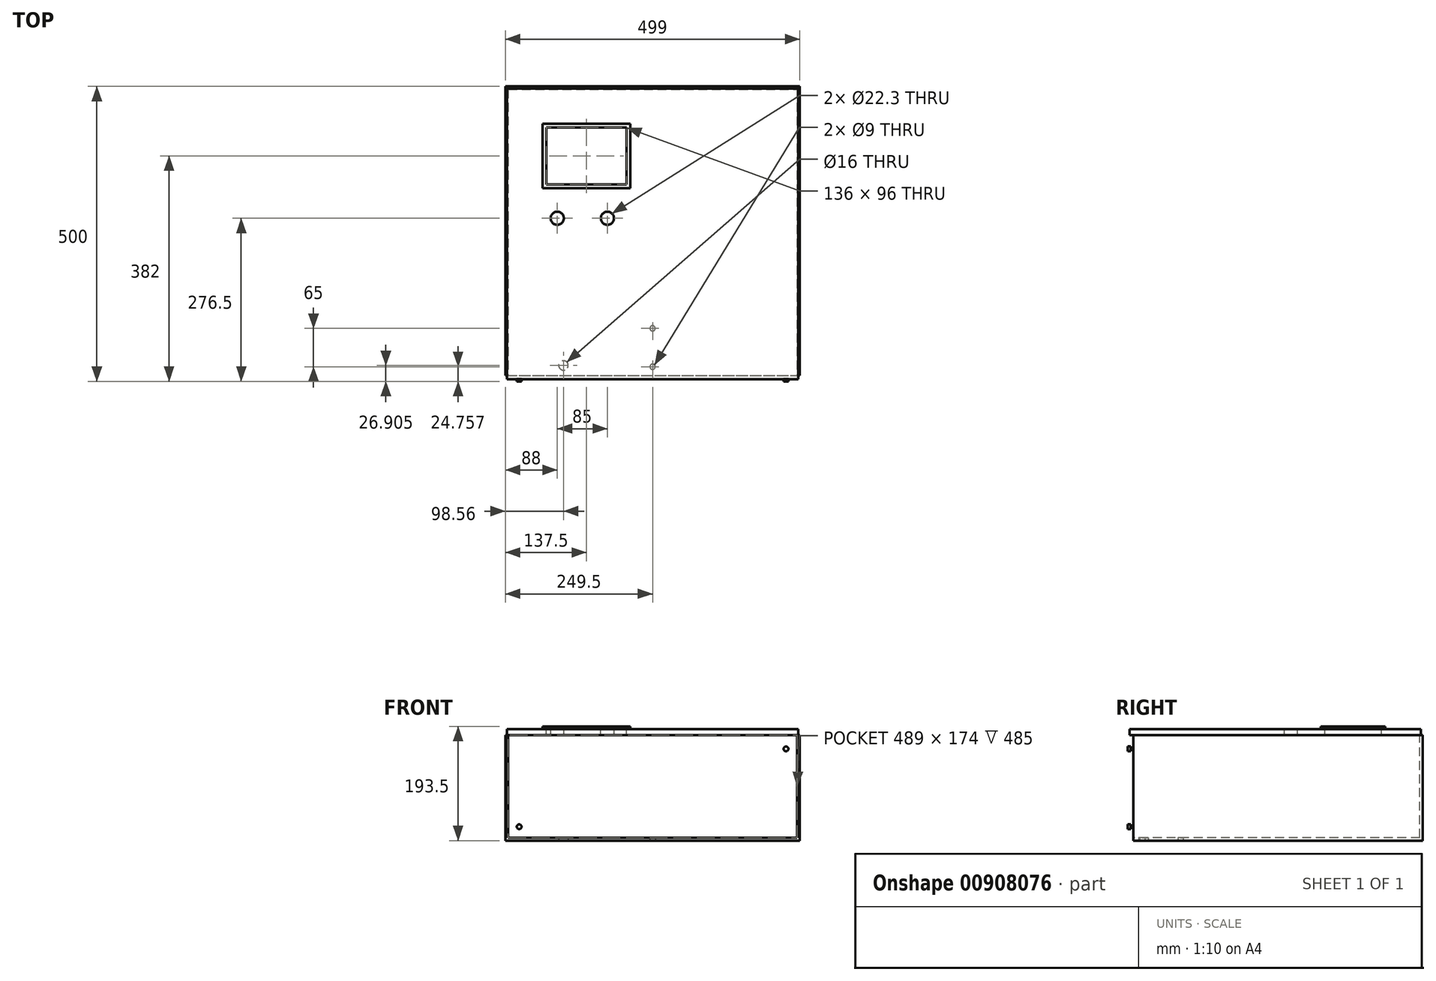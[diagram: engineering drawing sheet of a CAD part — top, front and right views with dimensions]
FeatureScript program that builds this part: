
annotation { "Feature Type Name" : "Feature", "Feature Type Description" : "" }
export const myFeature = defineFeature(function(context is Context, id is Id, definition is map)
    precondition{}
    {
        {
            var Q0;
            Q0=qCreatedBy(makeId("Top.planeOp"),FACE);
            var sketch = newSketch(context, id + "F0", { "sketchPlane" : qUnion([Q0])});
            skLineSegment(sketch, "E0.bottom", {"start": v(-249.5, 250) * mm, "end": v(249.5, 250) * mm});
            skLineSegment(sketch, "E0.top", {"start": v(-249.5, -250) * mm, "end": v(249.5, -250) * mm});
            skLineSegment(sketch, "E0.left", {"start": v(-249.5, 250) * mm, "end": v(-249.5, -250) * mm});
            skLineSegment(sketch, "E0.right", {"start": v(249.5, 250) * mm, "end": v(249.5, -250) * mm});
            skPoint(sketch, "E0.middle", {"position": v(0, 0) * mm});
            skSolve(sketch);
        }
        {
            var Q0;
            Q0=makeQuery(id+"F0.imprint","IMPRINT",FACE,{"disambiguationData":[TD([[makeQuery(id+"F0.imprint","IMPRINT",EDGE,{"derivedFrom":sQuery(id+"F0.wireOp",EDGE,"E0.bottom")}),-1.0]])]});
            extrude(context, id + "F1", {"entities" : qUnion([Q0]), "oppositeDirection" : true, "depth" : 179 * mm, "offsetDistance" : 25 * mm});
        }
        {
            var Q0;
            Q0=makeQuery(id+"F1.opExtrude","CAP_FACE",FACE,{"disambiguationData":[OSD([sQuery(id+"F0.wireOp",EDGE,"E0.bottom"),sQuery(id+"F0.wireOp",EDGE,"E0.top"),sQuery(id+"F0.wireOp",EDGE,"E0.left"),sQuery(id+"F0.wireOp",EDGE,"E0.right")])],"isStart":true});
            shell(context, id + "F2", {"entities" : qUnion([Q0]), "thickness" : 5 * mm});
        }
        {
            var Q0;
            Q0=qCreatedBy(makeId("Top.planeOp"),FACE);
            var sketch = newSketch(context, id + "F3", { "sketchPlane" : qUnion([Q0])});
            skLineSegment(sketch, "E1.bottom", {"start": v(-246.5, 246.5) * mm, "end": v(246.5, 246.5) * mm});
            skLineSegment(sketch, "E1.top", {"start": v(-246.5, -246.5) * mm, "end": v(246.5, -246.5) * mm});
            skLineSegment(sketch, "E1.left", {"start": v(-246.5, 246.5) * mm, "end": v(-246.5, -246.5) * mm});
            skLineSegment(sketch, "E1.right", {"start": v(246.5, 246.5) * mm, "end": v(246.5, -246.5) * mm});
            skSolve(sketch);
        }
        {
            var Q0;
            Q0=makeQuery(id+"F3.imprint","IMPRINT",FACE,{"disambiguationData":[TD([[makeQuery(id+"F3.imprint","IMPRINT",EDGE,{"derivedFrom":sQuery(id+"F3.wireOp",EDGE,"E1.bottom")}),-1.0]])]});
            extrude(context, id + "F4", {"entities" : qUnion([Q0]), "operationType" : NewBodyOperationType.ADD, "depth" : 10 * mm, "offsetDistance" : 25 * mm});
        }
        {
            var Q0;
            Q0=makeQuery(id+"F4.opExtrude","CAP_FACE",FACE,{"disambiguationData":[OSD([sQuery(id+"F3.wireOp",EDGE,"E1.bottom"),sQuery(id+"F3.wireOp",EDGE,"E1.top"),sQuery(id+"F3.wireOp",EDGE,"E1.left"),sQuery(id+"F3.wireOp",EDGE,"E1.right")])],"isStart":false});
            var sketch = newSketch(context, id + "F5", { "sketchPlane" : qUnion([Q0])});
            skLineSegment(sketch, "E2.bottom", {"start": v(-37.5, 77.5) * mm, "end": v(-186.5, 77.5) * mm});
            skLineSegment(sketch, "E2.top", {"start": v(-37.5, 186.5) * mm, "end": v(-186.5, 186.5) * mm});
            skLineSegment(sketch, "E2.left", {"start": v(-37.5, 77.5) * mm, "end": v(-37.5, 186.5) * mm});
            skLineSegment(sketch, "E2.right", {"start": v(-186.5, 77.5) * mm, "end": v(-186.5, 186.5) * mm});
            skLineSegment(sketch, "E3.bottom", {"start": v(-227.5, 227.5) * mm, "end": v(227.5, 227.5) * mm, "construction": true});
            skLineSegment(sketch, "E3.top", {"start": v(-227.5, -227.5) * mm, "end": v(227.5, -227.5) * mm, "construction": true});
            skLineSegment(sketch, "E3.left", {"start": v(-227.5, 227.5) * mm, "end": v(-227.5, -227.5) * mm, "construction": true});
            skLineSegment(sketch, "E3.right", {"start": v(227.5, 227.5) * mm, "end": v(227.5, -227.5) * mm, "construction": true});
            skPoint(sketch, "E3.middle", {"position": v(0, 0) * mm});
            skLineSegment(sketch, "E4", {"start": v(12.5, 227.5) * mm, "end": v(12.5, -227.5) * mm, "construction": true});
            skSolve(sketch);
        }
        {
            var Q0;
            Q0=makeQuery(id+"F5.imprint","IMPRINT",FACE,{"disambiguationData":[TD([[makeQuery(id+"F5.imprint","IMPRINT",EDGE,{"derivedFrom":sQuery(id+"F5.wireOp",EDGE,"E2.bottom")}),-1.0]])]});
            extrude(context, id + "F6", {"entities" : qUnion([Q0]), "operationType" : NewBodyOperationType.ADD, "depth" : 4.5 * mm, "offsetDistance" : 25 * mm});
        }
        {
            var Q0;
            Q0=makeQuery(id+"F6.opExtrude","CAP_FACE",FACE,{"disambiguationData":[OSD([sQuery(id+"F5.wireOp",EDGE,"E2.bottom"),sQuery(id+"F5.wireOp",EDGE,"E2.top"),sQuery(id+"F5.wireOp",EDGE,"E2.left"),sQuery(id+"F5.wireOp",EDGE,"E2.right")])],"isStart":false});
            var sketch = newSketch(context, id + "F7", { "sketchPlane" : qUnion([Q0])});
            skLineSegment(sketch, "E5.bottom", {"start": v(-44, 180) * mm, "end": v(-180, 180) * mm});
            skLineSegment(sketch, "E5.top", {"start": v(-44, 84) * mm, "end": v(-180, 84) * mm});
            skLineSegment(sketch, "E5.left", {"start": v(-44, 180) * mm, "end": v(-44, 84) * mm});
            skLineSegment(sketch, "E5.right", {"start": v(-180, 180) * mm, "end": v(-180, 84) * mm});
            skPoint(sketch, "E5.middle", {"position": v(-112, 132) * mm});
            skPoint(sketch, "E5.middle.positionSnap0", {"position": v(-112, 77.5) * mm});
            skPoint(sketch, "E5.middle.positionSnap1", {"position": v(-186.5, 132) * mm});
            skPoint(sketch, "E5.centerSnap0", {"position": v(-112, 77.5) * mm});
            skPoint(sketch, "E5.centerSnap1", {"position": v(-186.5, 132) * mm});
            skSolve(sketch);
        }
        {
            var Q0;
            Q0=makeQuery(id+"F7.imprint","IMPRINT",FACE,{"disambiguationData":[TD([[makeQuery(id+"F7.imprint","IMPRINT",EDGE,{"derivedFrom":sQuery(id+"F7.wireOp",EDGE,"E5.bottom")}),1.0]])]});
            extrude(context, id + "F8", {"entities" : qUnion([Q0]), "operationType" : NewBodyOperationType.REMOVE, "oppositeDirection" : true, "depth" : 60.5 * mm, "offsetDistance" : 25 * mm});
        }
        {
            var Q0;
            Q0=makeQuery(id+"F4.opExtrude","CAP_FACE",FACE,{"disambiguationData":[OSD([sQuery(id+"F3.wireOp",EDGE,"E1.bottom"),sQuery(id+"F3.wireOp",EDGE,"E1.top"),sQuery(id+"F3.wireOp",EDGE,"E1.left"),sQuery(id+"F3.wireOp",EDGE,"E1.right")])],"isStart":false});
            var sketch = newSketch(context, id + "F9", { "sketchPlane" : qUnion([Q0])});
            skCircle(sketch, "E6", {"center": v(-76.5, 26.5) * mm, "radius": 11.15 * mm});
            skCircle(sketch, "E7", {"center": v(-161.5, 26.5) * mm, "radius": 11.15 * mm});
            skCircle(sketch, "E8", {"center": v(-76.5, 26.5) * mm, "radius": 27.5 * mm, "construction": true});
            skLineSegment(sketch, "E9.bottom", {"start": v(-176.5, 51.5) * mm, "end": v(-146.5, 51.5) * mm, "construction": true});
            skLineSegment(sketch, "E9.top", {"start": v(-176.5, 11.5) * mm, "end": v(-146.5, 11.5) * mm, "construction": true});
            skLineSegment(sketch, "E9.left", {"start": v(-176.5, 51.5) * mm, "end": v(-176.5, 11.5) * mm, "construction": true});
            skLineSegment(sketch, "E9.right", {"start": v(-146.5, 51.5) * mm, "end": v(-146.5, 11.5) * mm, "construction": true});
            skSolve(sketch);
        }
        {
            var Q0;
            Q0=makeQuery(id+"F9.imprint","IMPRINT",FACE,{"disambiguationData":[TD([[makeQuery(id+"F9.imprint","IMPRINT",EDGE,{"derivedFrom":sQuery(id+"F9.wireOp",EDGE,"E6")}),1.0]])]});
            var Q1;
            Q1=makeQuery(id+"F9.imprint","IMPRINT",FACE,{"disambiguationData":[TD([[makeQuery(id+"F9.imprint","IMPRINT",EDGE,{"derivedFrom":sQuery(id+"F9.wireOp",EDGE,"E7")}),1.0]])]});
            extrude(context, id + "F10", {"entities" : qUnion([Q0, Q1]), "operationType" : NewBodyOperationType.REMOVE, "oppositeDirection" : true, "depth" : 25 * mm, "offsetDistance" : 25 * mm});
        }
        {
            var Q0;
            Q0=makeQuery(id+"F1.opExtrude","CAP_FACE",FACE,{"disambiguationData":[OSD([sQuery(id+"F0.wireOp",EDGE,"E0.bottom"),sQuery(id+"F0.wireOp",EDGE,"E0.top"),sQuery(id+"F0.wireOp",EDGE,"E0.left"),sQuery(id+"F0.wireOp",EDGE,"E0.right")])],"isStart":false});
            var sketch = newSketch(context, id + "F11", { "sketchPlane" : qUnion([Q0])});
            skCircle(sketch, "E10", {"center": v(-150.94, 223.1) * mm, "radius": 8 * mm});
            skCircle(sketch, "E11", {"center": v(0, 160.24) * mm, "radius": 4.5 * mm});
            skCircle(sketch, "E12", {"center": v(0, 225.24) * mm, "radius": 4.5 * mm});
            skLineSegment(sketch, "E13.bottom", {"start": v(-20, 280.24) * mm, "end": v(20, 280.24) * mm, "construction": true});
            skLineSegment(sketch, "E13.top", {"start": v(-20, 120.24) * mm, "end": v(20, 120.24) * mm, "construction": true});
            skLineSegment(sketch, "E13.left", {"start": v(-20, 280.24) * mm, "end": v(-20, 120.24) * mm, "construction": true});
            skLineSegment(sketch, "E13.right", {"start": v(20, 280.24) * mm, "end": v(20, 120.24) * mm, "construction": true});
            skPoint(sketch, "E13.middle", {"position": v(0, 200.24) * mm});
            skSolve(sketch);
        }
        {
            var Q0;
            Q0=makeQuery(id+"F11.imprint","IMPRINT",FACE,{"disambiguationData":[TD([[makeQuery(id+"F11.imprint","IMPRINT",EDGE,{"derivedFrom":sQuery(id+"F11.wireOp",EDGE,"E10")}),1.0]])]});
            var Q1;
            Q1=makeQuery(id+"F11.imprint","IMPRINT",FACE,{"disambiguationData":[TD([[makeQuery(id+"F11.imprint","IMPRINT",EDGE,{"derivedFrom":sQuery(id+"F11.wireOp",EDGE,"E11")}),1.0]])]});
            var Q2;
            Q2=makeQuery(id+"F11.imprint","IMPRINT",FACE,{"disambiguationData":[TD([[makeQuery(id+"F11.imprint","IMPRINT",EDGE,{"derivedFrom":sQuery(id+"F11.wireOp",EDGE,"E12")}),1.0]])]});
            extrude(context, id + "F12", {"entities" : qUnion([Q0, Q1, Q2]), "operationType" : NewBodyOperationType.REMOVE, "oppositeDirection" : true, "depth" : 25 * mm, "offsetDistance" : 25 * mm});
        }
        {
            var Q0;
            Q0=makeQuery(id+"F1.opExtrude","SWEPT_FACE",FACE,{"disambiguationData":[OSD([sQuery(id+"F0.wireOp",EDGE,"E0.top")])]});
            var sketch = newSketch(context, id + "F13", { "sketchPlane" : qUnion([Q0])});
            skCircle(sketch, "E14", {"center": v(-226, -23.5) * mm, "radius": 4 * mm});
            skCircle(sketch, "E15", {"center": v(-226, -23.5) * mm, "radius": 23.5 * mm, "construction": true});
            skLineSegment(sketch, "E16", {"start": v(0, 0) * mm, "end": v(0, -179) * mm, "construction": true});
            skPoint(sketch, "E16.startSnap0", {"position": v(0, 0) * mm});
            skPoint(sketch, "E16.endSnap0", {"position": v(0, 0) * mm});
            skCircle(sketch, "E17.MirrorC", {"center": v(226, -23.5) * mm, "radius": 23.5 * mm, "construction": true});
            skCircle(sketch, "E18.MirrorC", {"center": v(226, -23.5) * mm, "radius": 4 * mm});
            skLineSegment(sketch, "E19", {"start": v(-249.5, -89.5) * mm, "end": v(249.5, -89.5) * mm, "construction": true});
            skCircle(sketch, "E20.MirrorC", {"center": v(-226, -155.5) * mm, "radius": 4 * mm});
            skCircle(sketch, "E21.MirrorC", {"center": v(-226, -155.5) * mm, "radius": 23.5 * mm, "construction": true});
            skCircle(sketch, "E22.MirrorC", {"center": v(226, -155.5) * mm, "radius": 4 * mm});
            skCircle(sketch, "E23.MirrorC", {"center": v(226, -155.5) * mm, "radius": 23.5 * mm, "construction": true});
            skSolve(sketch);
        }
        {
            var Q0;
            Q0=makeQuery(id+"F13.imprint","IMPRINT",FACE,{"disambiguationData":[TD([[makeQuery(id+"F13.imprint","IMPRINT",EDGE,{"derivedFrom":sQuery(id+"F13.wireOp",EDGE,"E14")}),1.0]])]});
            var Q1;
            Q1=makeQuery(id+"F13.imprint","IMPRINT",FACE,{"disambiguationData":[TD([[makeQuery(id+"F13.imprint","IMPRINT",EDGE,{"derivedFrom":sQuery(id+"F13.wireOp",EDGE,"E20.MirrorC")}),-1.0]])]});
            var Q2;
            Q2=makeQuery(id+"F13.imprint","IMPRINT",FACE,{"disambiguationData":[TD([[makeQuery(id+"F13.imprint","IMPRINT",EDGE,{"derivedFrom":sQuery(id+"F13.wireOp",EDGE,"E22.MirrorC")}),1.0]])]});
            var Q3;
            Q3=makeQuery(id+"F13.imprint","IMPRINT",FACE,{"disambiguationData":[TD([[makeQuery(id+"F13.imprint","IMPRINT",EDGE,{"derivedFrom":sQuery(id+"F13.wireOp",EDGE,"E18.MirrorC")}),-1.0]])]});
            extrude(context, id + "F14", {"entities" : qUnion([Q0, Q1, Q2, Q3]), "operationType" : NewBodyOperationType.REMOVE, "oppositeDirection" : true, "depth" : 10 * mm, "offsetDistance" : 25 * mm});
        }
    });
